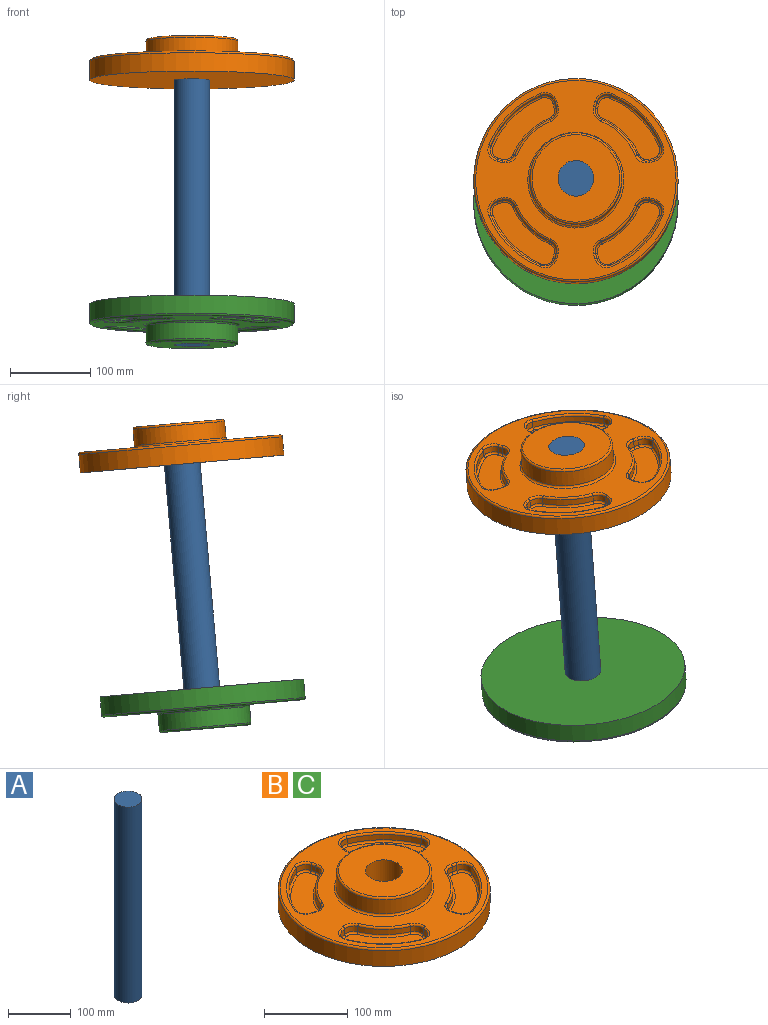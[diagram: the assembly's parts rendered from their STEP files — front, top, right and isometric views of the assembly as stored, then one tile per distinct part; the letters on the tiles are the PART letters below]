
ASSEMBLY  parts=3 mates=3
PART A: 3 faces, bbox 44.5x44.5x381 mm
  f0: cylinder r=22.23mm len=381mm, axis (0,0,-1), area 53204.3mm2, adj f1,f2
  f1: plane 44.45x44.45mm, normal (0,0,1), area 1551.8mm2, adj f0
  f2: plane 44.45x44.45mm, normal (0,0,-1), area 1551.8mm2, adj f0
PART B: 109 faces, bbox 274.9x274.9x50.8 mm
  f0: plane 248.92x248.92mm, normal (0,0,1), area 22339.7mm2, adj f41,f42,f43,f44,f45,f46,f47,f48
  f1: cylinder r=127mm len=254mm, axis (0,0,-1), area 18241.5mm2, adj f2,f107
  f2: plane 254x254mm, normal (0,0,-1), area 49119mm2, adj f1,f108
  f3: cylinder r=57.15mm len=114.3mm, axis (0,0,-1), area 7296.6mm2, adj f105,f106
  f4: plane 109.22x109.22mm, normal (0,0,1), area 7817.2mm2, adj f106,f108
  f5: cylinder r=12.7mm len=15.01mm, axis (0,0,1), area 139.1mm2, adj f6,f12,f94,f102
  f6: cylinder r=82.55mm len=44.37mm, axis (0,0,1), area 490.5mm2, adj f5,f7,f96,f104
  f7: cylinder r=12.7mm len=15.01mm, axis (0,0,1), area 139.1mm2, adj f6,f8,f95,f103
  f8: plane 7.62x6.19mm, normal (-0.97,-0.26,0), area 48.8mm2, adj f7,f9,f93,f101
  f9: cylinder r=12.7mm len=17.06mm, axis (0,0,1), area 164.1mm2, adj f8,f10,f91,f99
  f10: cylinder r=114.3mm len=62.69mm, axis (0,0,1), area 693.8mm2, adj f9,f11,f89,f97
  f11: cylinder r=12.7mm len=17.06mm, axis (0,0,1), area 164.1mm2, adj f10,f12,f90,f98
  f12: plane 7.62x6.19mm, normal (0.26,0.97,0), area 48.8mm2, adj f5,f11,f92,f100
  f13: plane 77.7x77.7mm, normal (0,0,1), area 2524mm2, adj f89,f90,f91,f92,f93,f94,f95,f96
  f14: plane 7.62x6.19mm, normal (-0.26,-0.97,0), area 48.8mm2, adj f15,f21,f41,f51
  f15: cylinder r=12.7mm len=15.01mm, axis (0,0,1), area 139.1mm2, adj f14,f16,f42,f49
  f16: cylinder r=82.55mm len=44.37mm, axis (0,0,1), area 490.5mm2, adj f15,f17,f44,f50
  f17: cylinder r=12.7mm len=15.01mm, axis (0,0,1), area 139.1mm2, adj f16,f18,f46,f52
  f18: plane 7.62x6.19mm, normal (0.97,0.26,0), area 48.8mm2, adj f17,f19,f48,f54
  f19: cylinder r=12.7mm len=17.06mm, axis (0,0,1), area 164.1mm2, adj f18,f20,f47,f56
  f20: cylinder r=114.3mm len=62.69mm, axis (0,0,1), area 693.8mm2, adj f19,f21,f45,f55
  f21: cylinder r=12.7mm len=17.06mm, axis (0,0,1), area 164.1mm2, adj f14,f20,f43,f53
  f22: plane 77.7x77.7mm, normal (0,0,1), area 2524mm2, adj f49,f50,f51,f52,f53,f54,f55,f56
  f23: cylinder r=12.7mm len=17.06mm, axis (0,0,1), area 164.1mm2, adj f24,f30,f59,f70
  f24: cylinder r=114.3mm len=62.69mm, axis (0,0,1), area 693.8mm2, adj f23,f25,f61,f72
  f25: cylinder r=12.7mm len=17.06mm, axis (0,0,1), area 164.1mm2, adj f24,f26,f63,f71
  f26: plane 7.62x6.19mm, normal (-0.97,0.26,0), area 48.8mm2, adj f25,f27,f64,f69
  f27: cylinder r=12.7mm len=15.01mm, axis (0,0,1), area 139.1mm2, adj f26,f28,f62,f67
  f28: cylinder r=82.55mm len=44.37mm, axis (0,0,1), area 490.5mm2, adj f27,f29,f60,f65
  f29: cylinder r=12.7mm len=15.01mm, axis (0,0,1), area 139.1mm2, adj f28,f30,f58,f66
  f30: plane 7.62x6.19mm, normal (0.26,-0.97,0), area 48.8mm2, adj f23,f29,f57,f68
  f31: plane 77.7x77.7mm, normal (0,0,1), area 2524mm2, adj f65,f66,f67,f68,f69,f70,f71,f72
  f32: cylinder r=12.7mm len=15.01mm, axis (0,0,1), area 139.1mm2, adj f33,f39,f77,f87
  f33: cylinder r=82.55mm len=44.37mm, axis (0,0,1), area 490.5mm2, adj f32,f34,f79,f88
  f34: cylinder r=12.7mm len=15.01mm, axis (0,0,1), area 139.1mm2, adj f33,f35,f80,f86
  f35: plane 7.62x6.19mm, normal (-0.26,0.97,0), area 48.8mm2, adj f34,f36,f78,f84
  f36: cylinder r=12.7mm len=17.06mm, axis (0,0,1), area 164.1mm2, adj f35,f37,f76,f82
  f37: cylinder r=114.3mm len=62.69mm, axis (0,0,1), area 693.8mm2, adj f36,f38,f74,f81
  f38: cylinder r=12.7mm len=17.06mm, axis (0,0,1), area 164.1mm2, adj f37,f39,f73,f83
  f39: plane 7.62x6.19mm, normal (0.97,-0.26,0), area 48.8mm2, adj f32,f38,f75,f85
  f40: plane 77.7x77.7mm, normal (0,0,1), area 2524mm2, adj f81,f82,f83,f84,f85,f86,f87,f88
  f41: cylinder r=2.54mm len=6.84mm, axis (0.97,-0.26,0), area 25.5mm2, adj f0,f14,f42,f43
  f42: torus R=15.24mm, axis (0,0,1), area 78.1mm2, adj f0,f15,f41,f44
  f43: torus R=15.24mm, axis (0,0,1), area 92.2mm2, adj f0,f21,f41,f45
  f44: torus R=80.01mm, axis (0,0,1), area 253.9mm2, adj f0,f16,f42,f46
  f45: torus R=116.84mm, axis (0,0,1), area 366.2mm2, adj f0,f20,f43,f47
  f46: torus R=15.24mm, axis (0,0,1), area 78.1mm2, adj f0,f17,f44,f48
  f47: torus R=15.24mm, axis (0,0,1), area 92.2mm2, adj f0,f19,f45,f48
  f48: cylinder r=2.54mm len=6.84mm, axis (-0.26,0.97,0), area 25.5mm2, adj f0,f18,f46,f47
  f49: torus R=10.16mm, axis (0,0,1), area 67.5mm2, adj f15,f22,f50,f51
  f50: torus R=85.09mm, axis (0,0,1), area 259.7mm2, adj f16,f22,f49,f52
  f51: cylinder r=2.54mm len=6.84mm, axis (-0.97,0.26,0), area 25.5mm2, adj f14,f22,f49,f53
  f52: torus R=10.16mm, axis (0,0,1), area 67.5mm2, adj f17,f22,f50,f54
  f53: torus R=10.16mm, axis (0,0,1), area 79.7mm2, adj f21,f22,f51,f55
  f54: cylinder r=2.54mm len=6.84mm, axis (0.26,-0.97,0), area 25.5mm2, adj f18,f22,f52,f56
  f55: torus R=111.76mm, axis (0,0,1), area 360.3mm2, adj f20,f22,f53,f56
  f56: torus R=10.16mm, axis (0,0,1), area 79.7mm2, adj f19,f22,f54,f55
  f57: cylinder r=2.54mm len=6.84mm, axis (0.97,0.26,0), area 25.5mm2, adj f0,f30,f58,f59
  f58: torus R=15.24mm, axis (0,0,1), area 78.1mm2, adj f0,f29,f57,f60
  f59: torus R=15.24mm, axis (0,0,1), area 92.2mm2, adj f0,f23,f57,f61
  f60: torus R=80.01mm, axis (0,0,1), area 253.9mm2, adj f0,f28,f58,f62
  f61: torus R=116.84mm, axis (0,0,1), area 366.2mm2, adj f0,f24,f59,f63
  f62: torus R=15.24mm, axis (0,0,1), area 78.1mm2, adj f0,f27,f60,f64
  f63: torus R=15.24mm, axis (0,0,1), area 92.2mm2, adj f0,f25,f61,f64
  f64: cylinder r=2.54mm len=6.84mm, axis (-0.26,-0.97,0), area 25.5mm2, adj f0,f26,f62,f63
  f65: torus R=85.09mm, axis (0,0,1), area 259.7mm2, adj f28,f31,f66,f67
  f66: torus R=10.16mm, axis (0,0,1), area 67.5mm2, adj f29,f31,f65,f68
  f67: torus R=10.16mm, axis (0,0,1), area 67.5mm2, adj f27,f31,f65,f69
  f68: cylinder r=2.54mm len=6.84mm, axis (-0.97,-0.26,0), area 25.5mm2, adj f30,f31,f66,f70
  f69: cylinder r=2.54mm len=6.84mm, axis (0.26,0.97,0), area 25.5mm2, adj f26,f31,f67,f71
  f70: torus R=10.16mm, axis (0,0,1), area 79.7mm2, adj f23,f31,f68,f72
  f71: torus R=10.16mm, axis (0,0,1), area 79.7mm2, adj f25,f31,f69,f72
  f72: torus R=111.76mm, axis (0,0,1), area 360.3mm2, adj f24,f31,f70,f71
  f73: torus R=15.24mm, axis (0,0,1), area 92.2mm2, adj f0,f38,f74,f75
  f74: torus R=116.84mm, axis (0,0,1), area 366.2mm2, adj f0,f37,f73,f76
  f75: cylinder r=2.54mm len=6.84mm, axis (0.26,0.97,0), area 25.5mm2, adj f0,f39,f73,f77
  f76: torus R=15.24mm, axis (0,0,1), area 92.2mm2, adj f0,f36,f74,f78
  f77: torus R=15.24mm, axis (0,0,1), area 78.1mm2, adj f0,f32,f75,f79
  f78: cylinder r=2.54mm len=6.84mm, axis (-0.97,-0.26,0), area 25.5mm2, adj f0,f35,f76,f80
  f79: torus R=80.01mm, axis (0,0,1), area 253.9mm2, adj f0,f33,f77,f80
  f80: torus R=15.24mm, axis (0,0,1), area 78.1mm2, adj f0,f34,f78,f79
  f81: torus R=111.76mm, axis (0,0,1), area 360.3mm2, adj f37,f40,f82,f83
  f82: torus R=10.16mm, axis (0,0,1), area 79.7mm2, adj f36,f40,f81,f84
  f83: torus R=10.16mm, axis (0,0,1), area 79.7mm2, adj f38,f40,f81,f85
  f84: cylinder r=2.54mm len=6.84mm, axis (0.97,0.26,0), area 25.5mm2, adj f35,f40,f82,f86
  f85: cylinder r=2.54mm len=6.84mm, axis (-0.26,-0.97,0), area 25.5mm2, adj f39,f40,f83,f87
  f86: torus R=10.16mm, axis (0,0,1), area 67.5mm2, adj f34,f40,f84,f88
  f87: torus R=10.16mm, axis (0,0,1), area 67.5mm2, adj f32,f40,f85,f88
  f88: torus R=85.09mm, axis (0,0,1), area 259.7mm2, adj f33,f40,f86,f87
  f89: torus R=111.76mm, axis (0,0,1), area 360.3mm2, adj f10,f13,f90,f91
  f90: torus R=10.16mm, axis (0,0,1), area 79.7mm2, adj f11,f13,f89,f92
  f91: torus R=10.16mm, axis (0,0,1), area 79.7mm2, adj f9,f13,f89,f93
  f92: cylinder r=2.54mm len=6.84mm, axis (0.97,-0.26,0), area 25.5mm2, adj f12,f13,f90,f94
  f93: cylinder r=2.54mm len=6.84mm, axis (-0.26,0.97,0), area 25.5mm2, adj f8,f13,f91,f95
  f94: torus R=10.16mm, axis (0,0,1), area 67.5mm2, adj f5,f13,f92,f96
  f95: torus R=10.16mm, axis (0,0,1), area 67.5mm2, adj f7,f13,f93,f96
  f96: torus R=85.09mm, axis (0,0,1), area 259.7mm2, adj f6,f13,f94,f95
  f97: torus R=116.84mm, axis (0,0,1), area 366.2mm2, adj f0,f10,f98,f99
  f98: torus R=15.24mm, axis (0,0,1), area 92.2mm2, adj f0,f11,f97,f100
  f99: torus R=15.24mm, axis (0,0,1), area 92.2mm2, adj f0,f9,f97,f101
  f100: cylinder r=2.54mm len=6.84mm, axis (-0.97,0.26,0), area 25.5mm2, adj f0,f12,f98,f102
  f101: cylinder r=2.54mm len=6.84mm, axis (0.26,-0.97,0), area 25.5mm2, adj f0,f8,f99,f103
  f102: torus R=15.24mm, axis (0,0,1), area 78.1mm2, adj f0,f5,f100,f104
  f103: torus R=15.24mm, axis (0,0,1), area 78.1mm2, adj f0,f7,f101,f104
  f104: torus R=80.01mm, axis (0,0,1), area 253.9mm2, adj f0,f6,f102,f103
  f105: torus R=59.69mm, axis (0,0,1), area 1455.8mm2, adj f0,f3
  f106: torus R=54.61mm, axis (0,0,1), area 1409.5mm2, adj f3,f4
  f107: torus R=124.46mm, axis (0,0,1), area 3160.6mm2, adj f0,f1
  f108: cylinder r=22.23mm len=50.8mm, axis (0,0,1), area 7093.9mm2, adj f2,f4
PART C: same geometry as B
PLACE A rot(axis=(-1,0,0),5deg) t=(-288.64,-10.65,-266.73)mm
PLACE B rot(axis=(-1,0,0),5deg) t=(-72.93,-17.29,116.3)mm fixed
PLACE C rot(axis=(1,0,0),175deg) t=(-72.93,-41.64,-162.03)mm
MATE fastened A.f0 <-> C.f1  axis (0,-0.09,-1) through (-72.93,-46.07,-212.64)mm
MATE slider B.f1 <-> C.f1  axis (0,0.09,1) through (-72.93,-12.86,166.91)mm
MATE fastened A.f0 <-> B.f1  axis (0,0.09,1) through (-72.93,-12.86,166.91)mm
